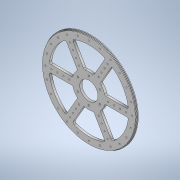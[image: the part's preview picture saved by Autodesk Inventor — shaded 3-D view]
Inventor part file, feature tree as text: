
AUTODESK INVENTOR PART (.ipt)
format: ipt  version: 2020 (Build 240168000, 168)  size: 359,424 bytes
history: native  units: in
note: dims shown in document units (in); Inventor stores cm internally (conversion verified against a paired STEP export)
features: extrude x4, sketch x4, fillet x1
ambient origin geometry x8: Origin, YZ Plane, XZ Plane, XY Plane, X Axis, Y Axis, Z Axis, Center Point
bodies: Solid1 (feature_tree)
feature tree (9):
  extrude  "Extrusion1"  Depth=2.125in
  fillet  "Fillet1"  Radius=2.125in
  extrude  "Extrusion2"  Depth=2.3622in TaperAngle=360.0deg
  extrude  "Extrusion3"  Depth=2.75in
  extrude  "Extrusion4"  Depth=1.25in
  sketch  "Sketch1"  dims[d0=15.75in d1=3.0236in d2=2.125in]
  sketch  "Sketch2"  dims[d3=0.2656in d4=2.3622in d6=360.0deg]
  sketch  "Sketch3"  dims[d8=6.625in d9=2.75in]
  sketch  "Sketch5"  dims[d10=2.3622in d12=360.0deg d14=1.25in d15=0.375in d16=0.0in d17=0.25in d18=0.0625in d19=0.25in d20=0.0in d21=0.0625in d22=0.125in d23=0.0in d24=0.203in d25=7.25in d26=1.9685in d28=1.0in d29=0.3937in d31=1.0in d33=2.3622in d35=360.0deg d37=9.4488in d39=360.0deg d41=0.0in d42=0.0in]
